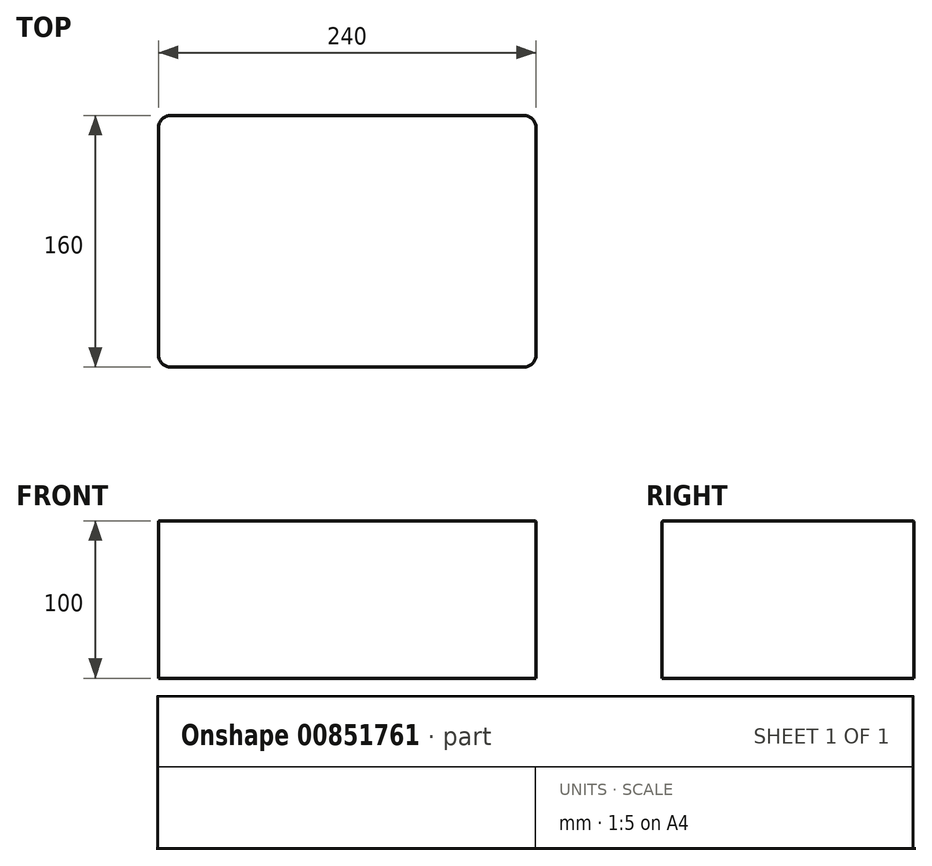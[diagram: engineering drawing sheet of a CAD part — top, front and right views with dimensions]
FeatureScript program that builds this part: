
annotation { "Feature Type Name" : "Feature", "Feature Type Description" : "" }
export const myFeature = defineFeature(function(context is Context, id is Id, definition is map)
    precondition{}
    {
        {
            var Q0;
            Q0=qCreatedBy(makeId("Top.planeOp"),FACE);
            var sketch = newSketch(context, id + "F0", { "sketchPlane" : qUnion([Q0])});
            skLineSegment(sketch, "E0.bottom", {"start": v(-120.1, 79.77) * mm, "end": v(119.9, 79.77) * mm});
            skLineSegment(sketch, "E0.top", {"start": v(-120.1, -80.23) * mm, "end": v(119.9, -80.23) * mm});
            skLineSegment(sketch, "E0.left", {"start": v(-120.1, 79.77) * mm, "end": v(-120.1, -80.23) * mm});
            skLineSegment(sketch, "E0.right", {"start": v(119.9, 79.77) * mm, "end": v(119.9, -80.23) * mm});
            skSolve(sketch);
        }
        {
            var Q0;
            Q0=makeQuery(id+"F0.imprint","IMPRINT",FACE,{"disambiguationData":[TD([[makeQuery(id+"F0.imprint","IMPRINT",EDGE,{"derivedFrom":sQuery(id+"F0.wireOp",EDGE,"E0.bottom")}),-1.0]])]});
            extrude(context, id + "F1", {"entities" : qUnion([Q0]), "depth" : 100 * mm, "offsetDistance" : 25 * mm});
        }
        {
            var Q0;
            Q0=makeQuery(id+"F1.opExtrude","SWEPT_EDGE",EDGE,{"disambiguationData":[OSD([sQuery(id+"F0.wireOp",EDGE,"E0.top"),sQuery(id+"F0.wireOp",EDGE,"E0.right")])]});
            var Q1;
            Q1=makeQuery(id+"F1.opExtrude","SWEPT_EDGE",EDGE,{"disambiguationData":[OSD([sQuery(id+"F0.wireOp",EDGE,"E0.top"),sQuery(id+"F0.wireOp",EDGE,"E0.left")])]});
            var Q2;
            Q2=makeQuery(id+"F1.opExtrude","SWEPT_EDGE",EDGE,{"disambiguationData":[OSD([sQuery(id+"F0.wireOp",EDGE,"E0.bottom"),sQuery(id+"F0.wireOp",EDGE,"E0.right")])]});
            var Q3;
            Q3=makeQuery(id+"F1.opExtrude","SWEPT_EDGE",EDGE,{"disambiguationData":[OSD([sQuery(id+"F0.wireOp",EDGE,"E0.bottom"),sQuery(id+"F0.wireOp",EDGE,"E0.left")])]});
            fillet(context, id + "F2", {"entities" : qUnion([Q0, Q1, Q2, Q3]), "radius" : 8 * mm, "tangentPropagation" : true, "allowEdgeOverflow" : false});
        }
        {
            var Q0;
            Q0=makeQuery(id+"F1.opExtrude","CAP_FACE",FACE,{"disambiguationData":[OSD([sQuery(id+"F0.wireOp",EDGE,"E0.bottom"),sQuery(id+"F0.wireOp",EDGE,"E0.top"),sQuery(id+"F0.wireOp",EDGE,"E0.left"),sQuery(id+"F0.wireOp",EDGE,"E0.right")])],"isStart":false});
            fillet(context, id + "F3", {"entities" : qUnion([Q0]), "radius" : 1 * mm, "tangentPropagation" : true, "allowEdgeOverflow" : false});
        }
    });
